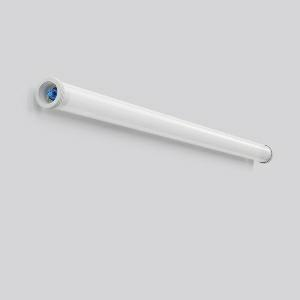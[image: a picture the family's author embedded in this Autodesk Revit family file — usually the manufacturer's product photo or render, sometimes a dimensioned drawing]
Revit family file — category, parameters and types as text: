
# Revit family: planox_tube_601072_002_1_730_a026
name_source: partatom
category: Lighting Fixtures
units: mm (PartAtom-declared; Revit-internal decimal feet)

## family parameters
Cut with Voids When Loaded = No
Host = Face
Light Source = No
Part Type = Normal
Room Calculation Point = No
Round Connector Dimension = Use Diameter
Shared = No

## types (1)
- PLANOX TUBE (1 x LED Modul 840, 8650 lm, 4000)
    Apparent Load = 62 VA
    CIE Flux Codes = 42 71 90 91 100
    Color Rendering = 80
    Color Temperature = 4000
    Default Elevation = 1800 mm
    Description = Series: PLANOX TUBE
Robust protective tube luminaire for tough requirements. Rack made of sheet steel, white powder coated. End caps made of plastic (polyamide) grey. Diffuser made of plastic (polycarbonate), opal, shockproof. Symmetrical light distribution. Homogeneous light distribution. With accessories for wall, ceiling or pendant mounting. Driver integrated. Easy installation with the Plug+Play Wieland RST CLASSIC plug-in system. Luminaire with integrated through-wiring for series connection of further luminaires by two Wieland RST Classic plug connectors (plug and socket). With Casambi smart+free Bluetooth control for wireless network and operation using Android / iOS devices, free app available for download. Accessories for electrical connection must be ordered separately. Mounting set must be ordered separately. Luminaire with limited surface temperature in accordance with EN 60598-2-24 for use in environments in which a deposit of conductive dust on the luminaire can be expected. Qualified for use in the food and drink industry. Suitable for lighting in public car parks and public off-street parking spaces according to DIN 67528. Environmentally friendly and resource-saving due to replaceable components. 
Colour: white
Diameter: 78 mm
Length: 1564 mm
Lamp: LED
Socket: without socket
Colour temperature: 4000K
Colour rendering index (CRI): 83
System power: 62 W
Rated luminous flux: 8650 lm
Luminous efficiency: 140 lm/W
Control gear: Dimmable Bluetooth converter
Protection class: I
Type of protection: IP 67
    Height = 0 mm  [stored 0 ft]
    Lamp = 1 x LED Modul 840
    Lamp Light Flux = 8650 lm
    Lamp count = 1
    Length = 1564 mm
    Lifetime = 50000 h
    Luminous efficacy = 140 lm/W
    Manufacturer = RZB
    ModVariant = No
    Model = 601072.002.1.730
    Mounting Place = Ceiling
    Mounting Type = Surface mounted
    Number of Poles = 1
    OnlyDefault = Yes
    Power Factor = 1
    Product Name = PLANOX TUBE
    Product group = Surface mounted luminaires for moist/humid enviroments
    ProductGroupID = 308
    Protection Class = Protection class I
    Protection Degree = Degree of protection
    RLX_Detail_Level = 1
    RLX_Emergency_Light_Flux = 0 lm
    RLX_Emergency_Type = 0
    RLX_Emergency_Type_DB = No
    RlxData = <blob elided: 35329 chars, md5=6cf1afac>
    Socket = socket
    Standby Power = 0 W
    System Light Flux = 8650 lm
    System Power = 62 W
    Type Comments = Product without accessories
    Type Image = 601072.002.jpg
    URL = http://relux.com
    VarID = ---
    Voltage = 0 V
    Weight = 0.00 kg
    Width = 0 mm  [stored 0 ft]

note: [stored X ft] marks values corroborated as IEEE doubles in the binary element streams (Revit-internal decimal feet)

## geometry (parser evidence)
native form markers: Blend x4, Sweep x11
no freeform markers — native parametric forms only
